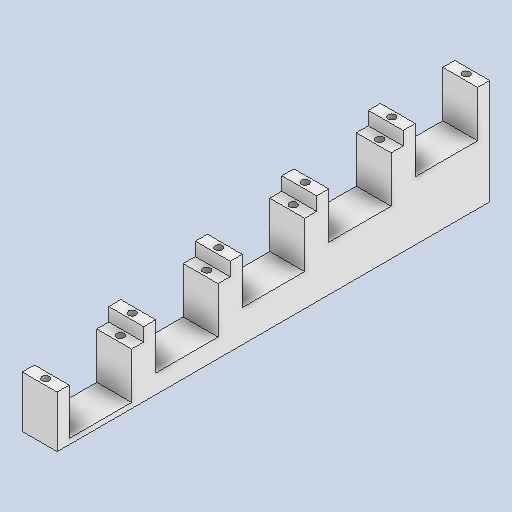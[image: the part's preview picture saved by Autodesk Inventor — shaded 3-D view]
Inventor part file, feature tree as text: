
AUTODESK INVENTOR PART (.ipt)
format: ipt  version: 2022 (Build 260153000, 153)  size: 292,352 bytes
history: native  units: in
note: dims shown in document units (in); Inventor stores cm internally (conversion verified against a paired STEP export)
features: extrude x10, thread x10, sketch x9, hole x5, plane x4
ambient origin geometry x8: Origin, YZ Plane, XZ Plane, XY Plane, X Axis, Y Axis, Z Axis, Center Point
bodies: Body1 (feature_tree)
feature tree (38):
  extrude  "Extrusion15"  Depth=6.2992in
  extrude  "Extrusion16"  Depth=0.6791in TaperAngle=0.0deg
  extrude  "Extrusion20"  Depth=0.1772in
  extrude  "Extrusion21"  Depth=0.1772in
  extrude  "Extrusion22"  Depth=0.1772in
  extrude  "Extrusion23"  Depth=1.2697in TaperAngle=0.0deg
  extrude  "Extrusion27"  Depth=0.1772in
  extrude  "Extrusion28"  Depth=1.4665in TaperAngle=0.0deg
  extrude  "Extrusion29"  Depth=0.1969in TaperAngle=0.0deg
  extrude  "Extrusion30"  Depth=0.3937in TaperAngle=0.0deg
  plane  "Work Plane1"
  plane  "Work Plane4"
  hole  "Hole1"  [1 undecoded]
  hole  "Hole2"  [1 undecoded]
  hole  "Hole3"  [1 undecoded]
  hole  "Hole4"  [1 undecoded]
  hole  "Hole5"  [1 undecoded]
  thread  "Thread1"  [1 undecoded]
  thread  "Thread2"  [1 undecoded]
  thread  "Thread3"  [1 undecoded]
  thread  "Thread4"  [1 undecoded]
  thread  "Thread5"  [1 undecoded]
  thread  "Thread6"  [1 undecoded]
  thread  "Thread7"  [1 undecoded]
  thread  "Thread8"  [1 undecoded]
  thread  "Thread9"  [1 undecoded]
  thread  "Thread10"  [1 undecoded]
  sketch  "Sketch15"  dims[d75=0.5118in d76=6.2992in]
  sketch  "Sketch21"  dims[d77=0.0787in d78=0.0in d84=0.6791in d85=0.0in]
  sketch  "Sketch27"  dims[d95=0.1772in d96=0.1102in]
  sketch  "Sketch28"  dims[d100=0.876in d101=0.0in d102=0.1772in]
  sketch  "Sketch29"  dims[d108=1.0728in d109=0.0in d110=0.1772in]
  sketch  "Sketch30"  dims[d111=0.1102in d116=1.2697in d117=0.0in]
  plane  "Work Plane2"
  plane  "Work Plane3"
  sketch  "Sketch35"  dims[d118=0.1772in d119=0.1102in]
  sketch  "Sketch38"  dims[d124=0.1772in d125=1.4665in d126=0.0in]
  sketch  "Sketch39"  dims[d127=0.0591in d143=0.1969in d144=0.0in d145=0.3937in d146=0.0in d147=0.5906in d148=0.0in d149=0.7874in d150=0.0in d164=-0.0591in d165=6.3583in d166=-2.5433in d167=-2.5433in d168=0.0886in d169=1.0945in d170=0.1102in d171=0.2362in d172=0.1575in d173=0.0787in d174=90.0deg d175=0.1181in d176=0.0in d179=0.1102in d180=0.2362in d181=0.1575in d182=0.0787in d183=90.0deg d184=0.1181in d185=0.0in d188=0.1102in d189=0.2362in d190=0.1575in d191=0.0787in d192=90.0deg d193=0.1181in d194=0.0in d195=0.0886in d196=1.0945in d197=0.1102in d198=0.2362in d199=0.1575in d200=0.0787in d201=90.0deg d202=0.1181in d203=0.0in d204=0.0886in d205=1.0945in d206=0.1102in d207=0.2362in d208=0.1575in d209=0.0787in d210=90.0deg d211=0.1181in d212=0.0in d235=0.2362in d236=0.0in d237=0.2362in d238=0.0in d239=0.2362in d240=0.0in d241=0.2362in d242=0.0in d243=0.2362in d244=0.0in d245=0.2362in d246=0.0in d247=0.2362in d248=0.0in d249=0.2362in d250=0.0in d251=0.2362in d252=0.0in d253=0.2362in d254=0.0in d64=0.0197in d65=0.0344in d66=0.0197in d67=0.0344in]
note: 15 required parameter values undecoded (feature->parameter linkage not recoverable at this tier; creation-order binding heuristic only, values carry confidence <= 0.55)
